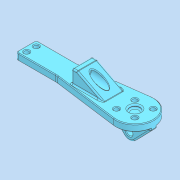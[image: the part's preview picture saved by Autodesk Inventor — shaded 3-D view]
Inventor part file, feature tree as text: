
AUTODESK INVENTOR PART (.ipt)
format: ipt  version: 2021.2 (Build 252289000, 289)  size: 702,976 bytes
history: native  units: mm
features: fillet x8, other x4, chamfer x2
ambient origin geometry x8: Origin, YZ Plane, XZ Plane, XY Plane, X Axis, Y Axis, Z Axis, Center Point
bodies: Body1 (feature_tree)
feature tree (14):
  other  "Твёрдое тело.ipt"
  fillet  "Сопряжение1"  Radius=10.0mm
  chamfer  "Фаска1"  Distance=2.0mm
  chamfer  "Фаска2"  Distance=0.5mm Angle=45.0deg
  fillet  "Сопряжение2"  Radius=0.5mm
  fillet  "Сопряжение3"  Radius=1.0mm
  fillet  "Сопряжение9"  Radius=1.0mm
  fillet  "Сопряжение5"  Radius=1.0mm
  fillet  "Сопряжение6"  Radius=0.5mm
  fillet  "Сопряжение7"  Radius=1.0mm
  fillet  "Сопряжение8"  Radius=0.5mm
  other  "Ложечка::Твёрдое тело.ipt"
  other  "Элемент создания тегов1"
  other  "Твердое тело1"
